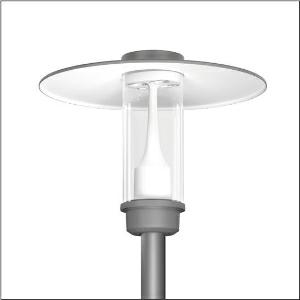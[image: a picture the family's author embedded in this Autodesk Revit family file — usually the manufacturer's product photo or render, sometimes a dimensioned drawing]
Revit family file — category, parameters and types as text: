
# Revit family: litepole_2_iq___p1_0a_5xa5425ff14h_a7e5
name_source: partatom
category: Lighting Fixtures
units: mm (PartAtom-declared; Revit-internal decimal feet)

## family parameters
Cut with Voids When Loaded = No
Host = Face
Light Source = No
Part Type = Normal
Room Calculation Point = No
Round Connector Dimension = Use Diameter
Shared = No

## types (1)
- --- (1 x LED, 1520 lm, 10.5 W, 3000K)
    Apparent Load = 11 VA
    CIE Flux Codes = 33 62 89 96 100
    Color Rendering = 70
    Color Temperature = 3000K
    Default Elevation = 1800 mm
    Description = Litepole 2 iQ, mast luminaire, Module 540 iQ-SR, primary light control with 3 zone facetted reflector, of plastic, silver coated, highly specular, structured, primary optical cover: cover, of PMMA, transparent, light distribution: P1.0a, light emission: direct distribution, primary light characteristic: strongly asymmetric, installation type: post-top, LED, High Power LED, rated luminous flux: 1.520lm, luminous efficacy: 145lm/W, light colour: 730, colour temperature: 3000K, control gear: ECG iQ, control: Auto-Match, Temp-Guard, Lumen-Switch, Night-Set, Smart-Wire, Light-Fading, Desk-Remote (wireless, voltage-free reading and setting of iQ features in the workshop via application-optimized NFC function/RFID function), optimised constant luminous flux control (CLO 2.0), Street-Remote, presetting dimming logarithmic, with terminal, 6-pole, max. 2.5mm², mains connection: 230..240V, AC, 50/60Hz, start of lifetime: 11W, end of service life: 11W, reduction: 5W, luminaire housing, upper part, of aluminium, coated, Siteco® metallic grey (DB 702S), diameter: 750mm, height: 590mm, spigot size: d x l = 76 x 70mm (post-top) | with reducer (optional accessory) 60 x 70mm, post-top mast mounting element, of diecast aluminium, coated, Siteco® metallic grey (DB 702S), Module 540 iQ-SR, traffic white (RAL 9016), equipment: standard, protection rating (complete): IP65, insulation class (complete): insulation class II (safety insulation), certification: CE, ENEC, VDE, packaging unit: 1 piece

Light Distribution: P1.0a
    Height = 590 mm
    Lamp = 1 x LED
    Lamp Light Flux = 1520 lm
    Lamp Power = 10.5 W
    Lamp count = 1
    Length = 750 mm
    Luminous efficacy = 145 lm/W
    Manufacturer = Siteco
    ModVariant = No
    Model = 5XA5425FF14H
    Number of Poles = 1
    OnlyDefault = Yes
    Power Factor = 1
    Product Name = Litepole 2 iQ | P1.0a
    Product group = mast luminaire | pylon top
    ProductGroupID = 6100
    Protection Class = Protection class II
    Protection Degree = IP 65
    RLX_Detail_Level = 1
    RLX_Emergency_Light_Flux = 0 lm
    RLX_Emergency_Type = 0
    RLX_Emergency_Type_DB = No
    RlxData = <blob elided: 138553 chars, md5=aa504196>
    Socket = socket
    Standby Power = 0 W
    System Light Flux = 1520 lm
    System Power = 11 W
    Type Comments = factory setting: luminous flux: 100 % | dim-lin: 254 | 419 mA
    Type Image = l_1006518.jpg
    URL = http://relux.com
    VarID = @adj_145157
    Voltage = 0 V
    Weight = 0.00 kg
    Width = 0 mm  [stored 0 ft]

note: [stored X ft] marks values corroborated as IEEE doubles in the binary element streams (Revit-internal decimal feet)

## geometry (parser evidence)
native form markers: Blend x4, Sweep x10
no freeform markers — native parametric forms only
